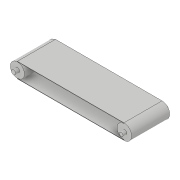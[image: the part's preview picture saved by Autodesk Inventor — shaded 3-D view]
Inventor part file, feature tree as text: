
AUTODESK INVENTOR PART (.ipt)
format: ipt  version: 2019 (Build 230136000, 136)  size: 131,072 bytes
history: native  units: in
note: dims shown in document units (in); Inventor stores cm internally (conversion verified against a paired STEP export)
features: sketch x10, extrude x9
ambient origin geometry x8: Origin, YZ Plane, XZ Plane, XY Plane, X Axis, Y Axis, Z Axis, Center Point
bodies: Solid1 (feature_tree)
feature tree (19):
  extrude  "Extrusion1"  Depth=55.1181in
  extrude  "Extrusion2"  Depth=55.1181in
  sketch  "Sketch3"  dims[d5=19.685in d6=0.0in d7=55.1181in]
  extrude  "Extrusion3"  Depth=55.1181in
  extrude  "Extrusion4"  Depth=19.685in TaperAngle=0.0deg
  extrude  "Extrusion5"  Depth=19.685in TaperAngle=0.0deg
  extrude  "Extrusion6"  Depth=1.9685in TaperAngle=0.0deg
  extrude  "Extrusion7"  Depth=1.9685in TaperAngle=0.0deg
  extrude  "Extrusion8"  [1 undecoded]
  extrude  "Extrusion9"  [1 undecoded]
  sketch  "Sketch1"  dims[d0=19.685in d1=0.0in d2=55.1181in]
  sketch  "Sketch2"  dims[d3=0.1969in d4=55.1181in]
  sketch  "Sketch4"  dims[d8=0.1969in d9=19.685in d10=0.0in]
  sketch  "Sketch5"  dims[d11=19.685in d12=0.0in d13=19.685in d14=0.0in]
  sketch  "Sketch6"  dims[d15=1.9685in d16=0.0in d17=1.9685in d18=0.0in]
  sketch  "Sketch7"  dims[d19=1.9685in d20=0.0in d21=1.9685in d22=0.0in]
  sketch  "Sketch8"
  sketch  "Sketch9"
  sketch  "Sketch10"
note: 2 required parameter values undecoded (feature->parameter linkage not recoverable at this tier; creation-order binding heuristic only, values carry confidence <= 0.55)
